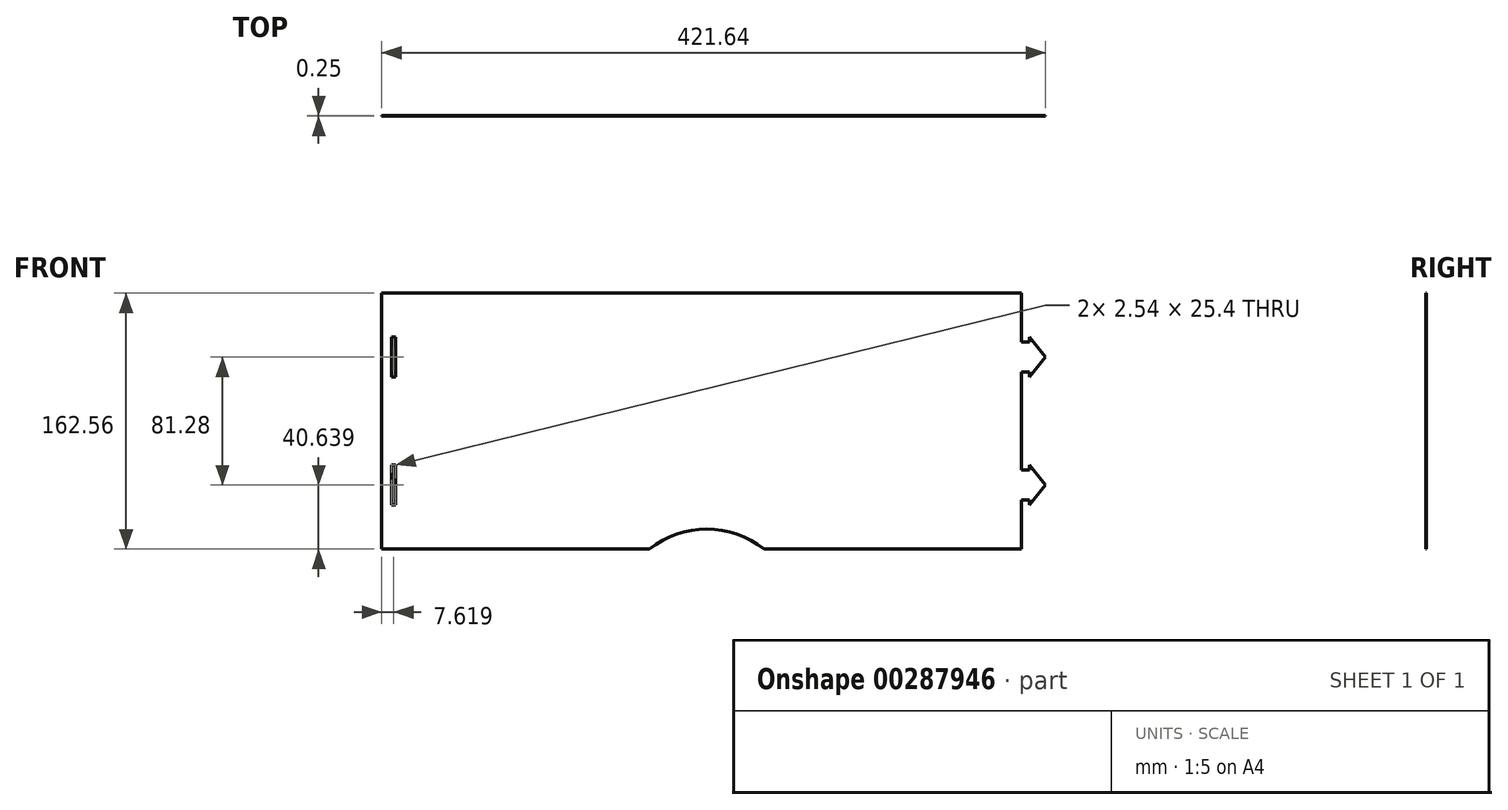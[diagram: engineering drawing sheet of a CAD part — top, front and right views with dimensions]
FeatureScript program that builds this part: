
annotation { "Feature Type Name" : "Feature", "Feature Type Description" : "" }
export const myFeature = defineFeature(function(context is Context, id is Id, definition is map)
    precondition{}
    {
        {
            var Q0;
            Q0=qCreatedBy(makeId("Front.planeOp"),FACE);
            var sketch = newSketch(context, id + "F0", { "sketchPlane" : qUnion([Q0])});
            skLineSegment(sketch, "E0.bottom", {"start": v(-206.41, 64.42) * mm, "end": v(199.99, 64.42) * mm});
            skLineSegment(sketch, "E0.top", {"start": v(-206.41, -98.14) * mm, "end": v(199.99, -98.14) * mm});
            skLineSegment(sketch, "E0.left", {"start": v(-206.41, 64.42) * mm, "end": v(-206.41, -98.14) * mm});
            skLineSegment(sketch, "E0.right", {"start": v(199.99, 64.42) * mm, "end": v(199.99, -98.14) * mm});
            skCircle(sketch, "E1", {"center": v(0, -143.86) * mm, "radius": 58.42 * mm});
            skLineSegment(sketch, "E2", {"start": v(0, 64.42) * mm, "end": v(0, -202.28) * mm, "construction": true});
            skLineSegment(sketch, "E3.bottom", {"start": v(199.99, -67.03) * mm, "end": v(205.07, -67.03) * mm});
            skLineSegment(sketch, "E3.top", {"start": v(199.99, -47.98) * mm, "end": v(205.07, -47.98) * mm});
            skLineSegment(sketch, "E3.left", {"start": v(199.99, -67.03) * mm, "end": v(199.99, -47.98) * mm});
            skLineSegment(sketch, "E3.right", {"start": v(205.07, -67.03) * mm, "end": v(205.07, -47.98) * mm});
            skLineSegment(sketch, "E4.bottom", {"start": v(199.99, 14.25) * mm, "end": v(205.07, 14.25) * mm});
            skLineSegment(sketch, "E4.top", {"start": v(199.99, 33.3) * mm, "end": v(205.07, 33.3) * mm});
            skLineSegment(sketch, "E4.left", {"start": v(199.99, 14.25) * mm, "end": v(199.99, 33.3) * mm});
            skLineSegment(sketch, "E4.right", {"start": v(205.07, 14.25) * mm, "end": v(205.07, 33.3) * mm});
            skLineSegment(sketch, "E5", {"start": v(-234.1, -16.86) * mm, "end": v(353.89, -16.86) * mm, "construction": true});
            skLineSegment(sketch, "E6", {"start": v(-235.02, 23.78) * mm, "end": v(364.51, 23.78) * mm, "construction": true});
            skLineSegment(sketch, "E7", {"start": v(-229.47, -57.5) * mm, "end": v(370.98, -57.5) * mm, "construction": true});
            skLineSegment(sketch, "E8", {"start": v(205.07, 33.3) * mm, "end": v(205.07, 36.48) * mm});
            skLineSegment(sketch, "E9", {"start": v(205.07, 36.48) * mm, "end": v(215.23, 23.78) * mm});
            skLineSegment(sketch, "E10", {"start": v(215.23, 23.78) * mm, "end": v(205.07, 11.08) * mm});
            skLineSegment(sketch, "E11", {"start": v(205.07, 11.08) * mm, "end": v(205.07, 14.25) * mm});
            skLineSegment(sketch, "E12.MirrorCS", {"start": v(215.23, -57.5) * mm, "end": v(205.07, -44.8) * mm});
            skLineSegment(sketch, "E13.MirrorCS", {"start": v(205.07, -70.2) * mm, "end": v(215.23, -57.5) * mm});
            skLineSegment(sketch, "E14.MirrorCS", {"start": v(205.07, -67.03) * mm, "end": v(205.07, -70.2) * mm});
            skLineSegment(sketch, "E15.MirrorCS", {"start": v(205.07, -44.8) * mm, "end": v(205.07, -47.98) * mm});
            skLineSegment(sketch, "E16.bottom", {"start": v(-197.52, 36.48) * mm, "end": v(-200.06, 36.48) * mm});
            skLineSegment(sketch, "E16.top", {"start": v(-197.52, 11.08) * mm, "end": v(-200.06, 11.08) * mm});
            skLineSegment(sketch, "E16.left", {"start": v(-197.52, 36.48) * mm, "end": v(-197.52, 11.08) * mm});
            skLineSegment(sketch, "E16.right", {"start": v(-200.06, 36.48) * mm, "end": v(-200.06, 11.08) * mm});
            skPoint(sketch, "E16.middle", {"position": v(-198.8, 23.78) * mm});
            skLineSegment(sketch, "E17.bottom", {"start": v(-200.06, -44.8) * mm, "end": v(-197.52, -44.8) * mm});
            skLineSegment(sketch, "E17.top", {"start": v(-200.06, -70.2) * mm, "end": v(-197.52, -70.2) * mm});
            skLineSegment(sketch, "E17.left", {"start": v(-200.06, -44.8) * mm, "end": v(-200.06, -70.2) * mm});
            skLineSegment(sketch, "E17.right", {"start": v(-197.52, -44.8) * mm, "end": v(-197.52, -70.2) * mm});
            skPoint(sketch, "E17.middle", {"position": v(-198.8, -57.5) * mm});
            skLineSegment(sketch, "E18.bottom", {"start": v(-44.45, 64.42) * mm, "end": v(44.45, 64.42) * mm});
            skLineSegment(sketch, "E18.top", {"start": v(-44.45, 140.62) * mm, "end": v(44.45, 140.62) * mm});
            skLineSegment(sketch, "E18.left", {"start": v(-44.45, 64.42) * mm, "end": v(-44.45, 140.62) * mm});
            skLineSegment(sketch, "E18.right", {"start": v(44.45, 64.42) * mm, "end": v(44.45, 140.62) * mm});
            skLineSegment(sketch, "E19.bottom", {"start": v(-19.05, 89.82) * mm, "end": v(19.05, 89.82) * mm});
            skLineSegment(sketch, "E19.top", {"start": v(-19.05, 115.22) * mm, "end": v(19.05, 115.22) * mm});
            skLineSegment(sketch, "E19.left", {"start": v(-19.05, 89.82) * mm, "end": v(-19.05, 115.22) * mm});
            skLineSegment(sketch, "E19.right", {"start": v(19.05, 89.82) * mm, "end": v(19.05, 115.22) * mm});
            skSolve(sketch);
        }
        {
            var Q0;
            {var subQ8=sQuery(id+"F0.wireOp",EDGE,"E0.bottom");Q0=makeQuery(id+"F0.imprint","IMPRINT",FACE,{"disambiguationData":[TD([[makeQuery(id+"F0.imprint","IMPRINT",EDGE,{"derivedFrom":subQ8}),-1.0]])]});}
            var Q1;
            Q1=makeQuery(id+"F0.imprint","IMPRINT",FACE,{"disambiguationData":[TD([[makeQuery(id+"F0.imprint","IMPRINT",EDGE,{"derivedFrom":sQuery(id+"F0.wireOp",EDGE,"E4.right")}),-1.0]])]});
            var Q2;
            Q2=makeQuery(id+"F0.imprint","IMPRINT",FACE,{"disambiguationData":[TD([[makeQuery(id+"F0.imprint","IMPRINT",EDGE,{"derivedFrom":sQuery(id+"F0.wireOp",EDGE,"E4.bottom")}),1.0]])]});
            var Q3;
            Q3=makeQuery(id+"F0.imprint","IMPRINT",FACE,{"disambiguationData":[TD([[makeQuery(id+"F0.imprint","IMPRINT",EDGE,{"derivedFrom":sQuery(id+"F0.wireOp",EDGE,"E3.bottom")}),1.0]])]});
            var Q4;
            Q4=makeQuery(id+"F0.imprint","IMPRINT",FACE,{"disambiguationData":[TD([[makeQuery(id+"F0.imprint","IMPRINT",EDGE,{"derivedFrom":sQuery(id+"F0.wireOp",EDGE,"E3.right")}),-1.0]])]});
            var Q5;
            {var subQ0=sQuery(id+"F0.wireOp",EDGE,"E1");var subQ1=sQuery(id+"F0.wireOp",EDGE,"E0.top");var subQ2=makeQuery(id+"F0.imprint","INTERSECT",VERTEX,{"disambiguationData":[OD(0.0)],"derivedFrom":[subQ1,subQ0]});Q5=makeQuery(id+"F0.imprint","IMPRINT",FACE,{"disambiguationData":[TD([[makeQuery(id+"F0.imprint","IMPRINT",EDGE,{"disambiguationData":[TD([[subQ2,-1.0]])],"derivedFrom":subQ1}),-1.0]])]});}
            var Q6;
            {var subQ0=sQuery(id+"F0.wireOp",EDGE,"E1");var subQ1=sQuery(id+"F0.wireOp",EDGE,"E0.top");var subQ2=makeQuery(id+"F0.imprint","INTERSECT",VERTEX,{"disambiguationData":[OD(0.0)],"derivedFrom":[subQ1,subQ0]});Q6=makeQuery(id+"F0.imprint","IMPRINT",FACE,{"disambiguationData":[TD([[makeQuery(id+"F0.imprint","IMPRINT",EDGE,{"disambiguationData":[TD([[subQ2,-1.0]])],"derivedFrom":subQ1}),1.0]])]});}
            var Q7;
            Q7=makeQuery(id+"F0.imprint","IMPRINT",FACE,{"disambiguationData":[TD([[makeQuery(id+"F0.imprint","IMPRINT",EDGE,{"derivedFrom":sQuery(id+"F0.wireOp",EDGE,"E18.bottom")}),1.0]])]});
            extrude(context, id + "F1", {"entities" : qUnion([Q0, Q1, Q2, Q3, Q4, Q5, Q6, Q7]), "depth" : 0.25 * mm});
        }
    });
